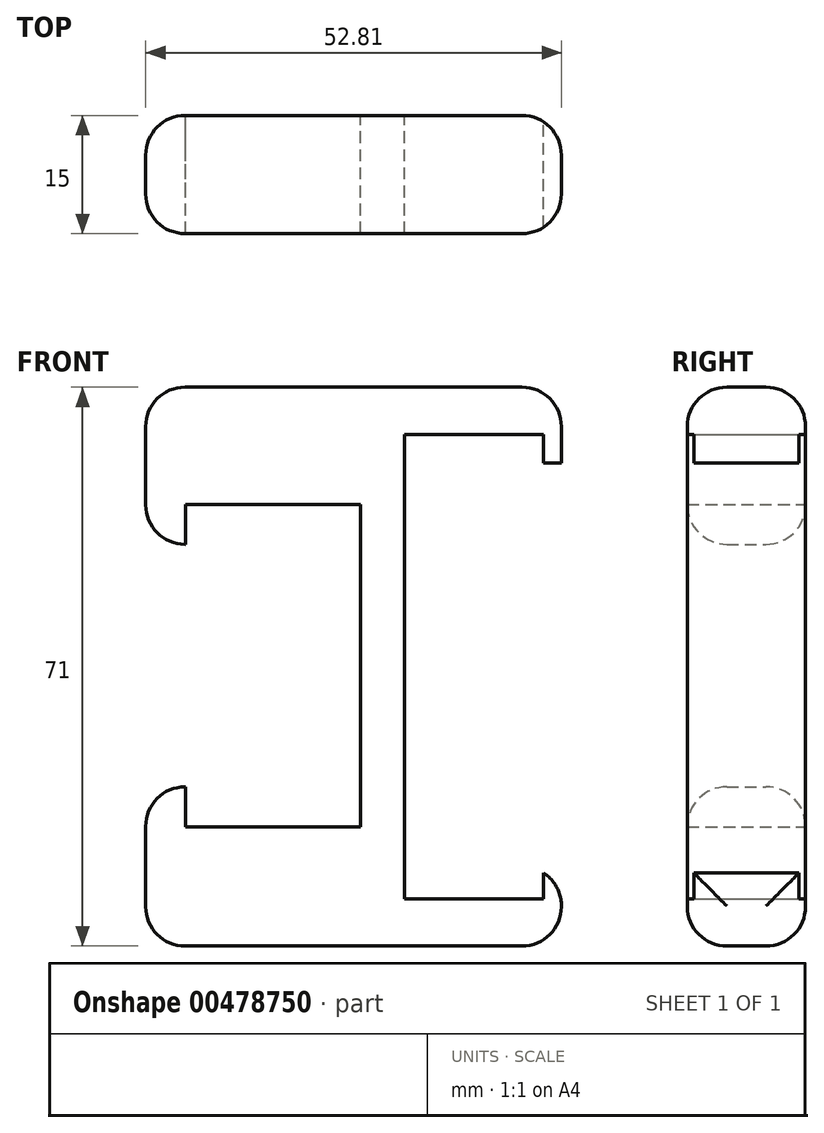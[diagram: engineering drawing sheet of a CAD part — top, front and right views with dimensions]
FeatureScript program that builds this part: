
annotation { "Feature Type Name" : "Feature", "Feature Type Description" : "" }
export const myFeature = defineFeature(function(context is Context, id is Id, definition is map)
    precondition{}
    {
        {
            var Q0;
            Q0=qCreatedBy(makeId("Front.planeOp"),FACE);
            var sketch = newSketch(context, id + "F0", { "sketchPlane" : qUnion([Q0])});
            skLineSegment(sketch, "E0", {"start": v(0, 46.8) * mm, "end": v(0, -18.2) * mm});
            skLineSegment(sketch, "E1", {"start": v(0, -18.2) * mm, "end": v(-32.85, -18.2) * mm});
            skLineSegment(sketch, "E2", {"start": v(-32.85, -18.2) * mm, "end": v(-32.85, 2.02) * mm});
            skLineSegment(sketch, "E3", {"start": v(-32.85, 2.02) * mm, "end": v(-27.8, 2.02) * mm});
            skLineSegment(sketch, "E4", {"start": v(-27.8, 2.02) * mm, "end": v(-27.8, -3.03) * mm});
            skLineSegment(sketch, "E5", {"start": v(-27.8, -3.03) * mm, "end": v(-5.56, -3.03) * mm});
            skLineSegment(sketch, "E6", {"start": v(-5.56, -3.03) * mm, "end": v(-5.56, 37.9) * mm});
            skLineSegment(sketch, "E7", {"start": v(-5.56, 37.9) * mm, "end": v(-27.8, 37.9) * mm});
            skLineSegment(sketch, "E8", {"start": v(-27.8, 37.9) * mm, "end": v(-27.8, 32.85) * mm});
            skLineSegment(sketch, "E9", {"start": v(-27.8, 32.85) * mm, "end": v(-32.85, 32.85) * mm});
            skLineSegment(sketch, "E10", {"start": v(-32.85, 32.85) * mm, "end": v(-32.85, 52.8) * mm});
            skPoint(sketch, "E10.endSnap0", {"position": v(-32.85, -8.09) * mm});
            skLineSegment(sketch, "E11", {"start": v(-32.85, 52.8) * mm, "end": v(0, 52.8) * mm});
            skLineSegment(sketch, "E12", {"start": v(0, 52.8) * mm, "end": v(0, -18.2) * mm});
            skLineSegment(sketch, "E13", {"start": v(0, -18.2) * mm, "end": v(19.96, -18.2) * mm});
            skLineSegment(sketch, "E14", {"start": v(19.96, -18.2) * mm, "end": v(19.96, -8.9) * mm});
            skLineSegment(sketch, "E15", {"start": v(19.96, -8.9) * mm, "end": v(17.69, -8.9) * mm});
            skLineSegment(sketch, "E16", {"start": v(17.69, -8.9) * mm, "end": v(17.69, -12.2) * mm});
            skLineSegment(sketch, "E17", {"start": v(17.69, -12.2) * mm, "end": v(0, -12.2) * mm});
            skLineSegment(sketch, "E18", {"start": v(0, 46.8) * mm, "end": v(17.69, 46.8) * mm});
            skLineSegment(sketch, "E19", {"start": v(0, 52.8) * mm, "end": v(19.96, 52.8) * mm});
            skLineSegment(sketch, "E20", {"start": v(19.96, 52.8) * mm, "end": v(19.96, 43.19) * mm});
            skPoint(sketch, "E20.endSnap0", {"position": v(19.96, -13.55) * mm});
            skLineSegment(sketch, "E21", {"start": v(19.96, 43.19) * mm, "end": v(17.69, 43.19) * mm});
            skLineSegment(sketch, "E22", {"start": v(17.69, 43.19) * mm, "end": v(17.69, 46.8) * mm});
            skSolve(sketch);
        }
        {
            var Q0;
            {var subQ0=sQuery(id+"F0.wireOp",EDGE,"E1");Q0=makeQuery(id+"F0.imprint","IMPRINT",FACE,{"disambiguationData":[TD([[makeQuery(id+"F0.imprint","IMPRINT",EDGE,{"derivedFrom":subQ0}),-1.0]])]});}
            var Q1;
            {var subQ1=sQuery(id+"F0.wireOp",EDGE,"E18");Q1=makeQuery(id+"F0.imprint","IMPRINT",FACE,{"disambiguationData":[TD([[makeQuery(id+"F0.imprint","IMPRINT",EDGE,{"derivedFrom":subQ1}),1.0]])]});}
            var Q2;
            {var subQ0=sQuery(id+"F0.wireOp",EDGE,"E13");Q2=makeQuery(id+"F0.imprint","IMPRINT",FACE,{"disambiguationData":[TD([[makeQuery(id+"F0.imprint","IMPRINT",EDGE,{"derivedFrom":subQ0}),1.0]])]});}
            extrude(context, id + "F1", {"entities" : qUnion([Q0, Q1, Q2]), "depth" : 15 * mm});
        }
        {
            var Q0;
            Q0=makeQuery(id+"F1.opExtrude","CAP_EDGE",EDGE,{"disambiguationData":[OSD([sQuery(id+"F0.wireOp",EDGE,"E11"),sQuery(id+"F0.wireOp",EDGE,"E19")])],"isStart":false});
            var Q1;
            Q1=makeQuery(id+"F1.opExtrude","CAP_EDGE",EDGE,{"disambiguationData":[OSD([sQuery(id+"F0.wireOp",EDGE,"E10")])],"isStart":false});
            var Q2;
            Q2=makeQuery(id+"F1.opExtrude","CAP_EDGE",EDGE,{"disambiguationData":[OSD([sQuery(id+"F0.wireOp",EDGE,"E2")])],"isStart":false});
            var Q3;
            Q3=makeQuery(id+"F1.opExtrude","CAP_EDGE",EDGE,{"disambiguationData":[OSD([sQuery(id+"F0.wireOp",EDGE,"E1"),sQuery(id+"F0.wireOp",EDGE,"E13")])],"isStart":false});
            var Q4;
            Q4=makeQuery(id+"F1.opExtrude","CAP_EDGE",EDGE,{"disambiguationData":[OSD([sQuery(id+"F0.wireOp",EDGE,"E14")])],"isStart":false});
            var Q5;
            Q5=makeQuery(id+"F1.opExtrude","CAP_EDGE",EDGE,{"disambiguationData":[OSD([sQuery(id+"F0.wireOp",EDGE,"E20")])],"isStart":false});
            var Q6;
            Q6=makeQuery(id+"F1.opExtrude","CAP_EDGE",EDGE,{"disambiguationData":[OSD([sQuery(id+"F0.wireOp",EDGE,"E10")])],"isStart":true});
            var Q7;
            Q7=makeQuery(id+"F1.opExtrude","CAP_EDGE",EDGE,{"disambiguationData":[OSD([sQuery(id+"F0.wireOp",EDGE,"E11"),sQuery(id+"F0.wireOp",EDGE,"E19")])],"isStart":true});
            var Q8;
            Q8=makeQuery(id+"F1.opExtrude","CAP_EDGE",EDGE,{"disambiguationData":[OSD([sQuery(id+"F0.wireOp",EDGE,"E20")])],"isStart":true});
            var Q9;
            Q9=makeQuery(id+"F1.opExtrude","CAP_EDGE",EDGE,{"disambiguationData":[OSD([sQuery(id+"F0.wireOp",EDGE,"E14")])],"isStart":true});
            var Q10;
            Q10=makeQuery(id+"F1.opExtrude","CAP_EDGE",EDGE,{"disambiguationData":[OSD([sQuery(id+"F0.wireOp",EDGE,"E1"),sQuery(id+"F0.wireOp",EDGE,"E13")])],"isStart":true});
            var Q11;
            Q11=makeQuery(id+"F1.opExtrude","CAP_EDGE",EDGE,{"disambiguationData":[OSD([sQuery(id+"F0.wireOp",EDGE,"E2")])],"isStart":true});
            var Q12;
            Q12=makeQuery(id+"F1.opExtrude","SWEPT_EDGE",EDGE,{"disambiguationData":[OSD([sQuery(id+"F0.wireOp",EDGE,"E19"),sQuery(id+"F0.wireOp",EDGE,"E20")])]});
            var Q13;
            Q13=makeQuery(id+"F1.opExtrude","SWEPT_EDGE",EDGE,{"disambiguationData":[OSD([sQuery(id+"F0.wireOp",EDGE,"E10"),sQuery(id+"F0.wireOp",EDGE,"E11")])]});
            var Q14;
            Q14=makeQuery(id+"F1.opExtrude","SWEPT_EDGE",EDGE,{"disambiguationData":[OSD([sQuery(id+"F0.wireOp",EDGE,"E1"),sQuery(id+"F0.wireOp",EDGE,"E2")])]});
            var Q15;
            Q15=makeQuery(id+"F1.opExtrude","SWEPT_FACE",FACE,{"disambiguationData":[OSD([sQuery(id+"F0.wireOp",EDGE,"E14")])]});
            fillet(context, id + "F2", {"entities" : qUnion([Q0, Q1, Q2, Q3, Q4, Q5, Q6, Q7, Q8, Q9, Q10, Q11, Q12, Q13, Q14, Q15]), "radius" : 5 * mm, "tangentPropagation" : true, "allowEdgeOverflow" : false});
        }
        {
            var Q0;
            Q0=makeQuery(id+"F2.opFillet","BLEND_EDGE",EDGE,{"blendedFrom":[makeQuery(id+"F1.opExtrude","CAP_EDGE",EDGE,{"disambiguationData":[OSD([sQuery(id+"F0.wireOp",EDGE,"E10")])],"isStart":false}),makeQuery(id+"F1.opExtrude","SWEPT_FACE",FACE,{"disambiguationData":[OSD([sQuery(id+"F0.wireOp",EDGE,"E9")])]})],"blendedInto":[makeQuery(id+"F1.opExtrude","SWEPT_FACE",FACE,{"disambiguationData":[OSD([sQuery(id+"F0.wireOp",EDGE,"E9")])]})]});
            var Q1;
            Q1=makeQuery(id+"F1.opExtrude","SWEPT_EDGE",EDGE,{"disambiguationData":[OSD([sQuery(id+"F0.wireOp",EDGE,"E2"),sQuery(id+"F0.wireOp",EDGE,"E3")])]});
            fillet(context, id + "F3", {"entities" : qUnion([Q0, Q1]), "radius" : 5 * mm, "tangentPropagation" : true, "allowEdgeOverflow" : false});
        }
    });
